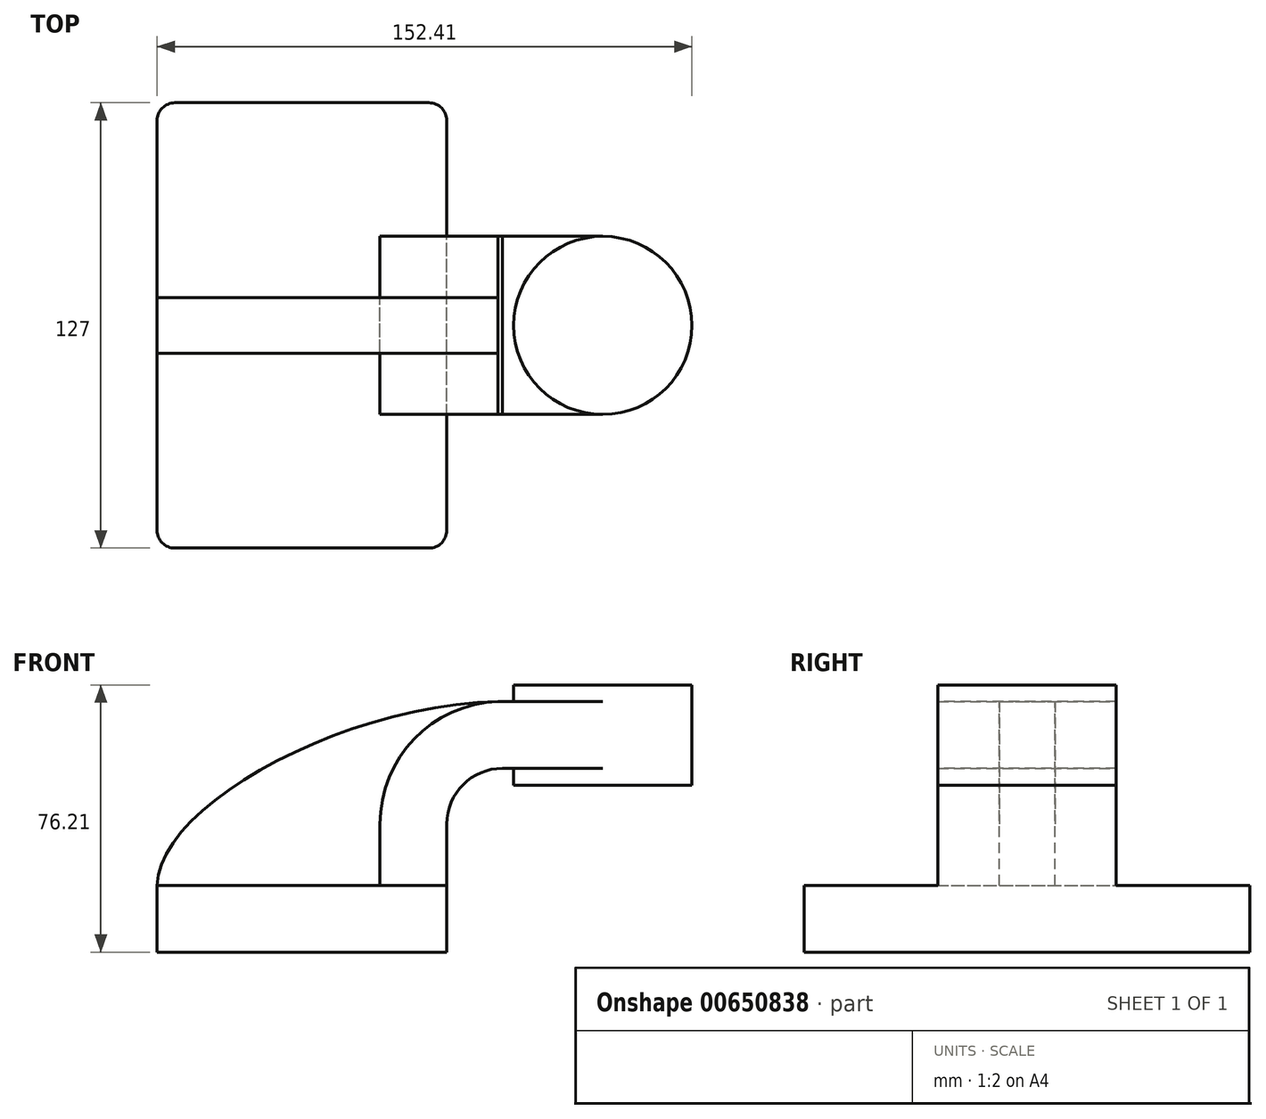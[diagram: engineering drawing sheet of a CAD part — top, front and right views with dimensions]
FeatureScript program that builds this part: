
annotation { "Feature Type Name" : "Feature", "Feature Type Description" : "" }
export const myFeature = defineFeature(function(context is Context, id is Id, definition is map)
    precondition{}
    {
        {
            var Q0;
            Q0=qCreatedBy(makeId("Front.planeOp"),FACE);
            var sketch = newSketch(context, id + "F0", { "sketchPlane" : qUnion([Q0])});
            skLineSegment(sketch, "E0.bottom", {"start": v(-41.28, -9.52) * mm, "end": v(41.28, -9.52) * mm});
            skLineSegment(sketch, "E0.top", {"start": v(-41.28, 9.53) * mm, "end": v(41.27, 9.53) * mm});
            skLineSegment(sketch, "E0.left", {"start": v(-41.27, -9.53) * mm, "end": v(-41.27, 9.52) * mm});
            skLineSegment(sketch, "E0.right", {"start": v(41.28, -9.53) * mm, "end": v(41.28, 9.52) * mm});
            skPoint(sketch, "E0.middle", {"position": v(0, 0) * mm});
            skLineSegment(sketch, "E1.bottom", {"start": v(60.32, 38.1) * mm, "end": v(111.12, 38.1) * mm});
            skLineSegment(sketch, "E1.top", {"start": v(60.32, 66.67) * mm, "end": v(111.12, 66.67) * mm});
            skLineSegment(sketch, "E1.left", {"start": v(60.32, 38.1) * mm, "end": v(60.32, 66.67) * mm});
            skLineSegment(sketch, "E1.right", {"start": v(111.12, 38.1) * mm, "end": v(111.12, 66.67) * mm});
            skPoint(sketch, "E1.middle", {"position": v(85.72, 52.39) * mm});
            skLineSegment(sketch, "E2", {"start": v(41.28, 9.52) * mm, "end": v(41.28, 27) * mm});
            skArc(sketch, "E3", {"start": v(41.27, 27) * mm, "mid": v(45.92, 38.23) * mm, "end": v(57.15, 42.88) * mm});
            skLineSegment(sketch, "E4", {"start": v(57.15, 42.88) * mm, "end": v(85.72, 42.88) * mm});
            skLineSegment(sketch, "E5.0", {"start": v(57.15, 61.93) * mm, "end": v(85.72, 61.93) * mm});
            skArc(sketch, "E5.1", {"start": v(22.22, 27) * mm, "mid": v(32.45, 51.7) * mm, "end": v(57.15, 61.93) * mm});
            skLineSegment(sketch, "E5.2", {"start": v(22.23, 9.53) * mm, "end": v(22.23, 27) * mm});
            skFitSpline(sketch, "E6", {"points": [v(-41.28, 9.53) * mm, v(57.15, 61.93) * mm], "startDerivative": vector(0.9, 67.4) * mm, "endDerivative": vector(137.17, 1.68) * mm});
            skLineSegment(sketch, "E7", {"start": v(85.72, 66.67) * mm, "end": v(85.72, 38.1) * mm});
            skSolve(sketch);
        }
        {
            var Q0;
            Q0=makeQuery(id+"F0.imprint","IMPRINT",FACE,{"disambiguationData":[TD([[makeQuery(id+"F0.imprint","IMPRINT",EDGE,{"derivedFrom":sQuery(id+"F0.wireOp",EDGE,"E0.bottom")}),1.0]])]});
            extrude(context, id + "F1", {"entities" : qUnion([Q0]), "endBound" : BoundingType.SYMMETRIC, "depth" : 127 * mm, "offsetDistance" : 25.4 * mm});
        }
        {
            var Q0;
            {var subQ1=sQuery(id+"F0.wireOp",EDGE,"E2");Q0=makeQuery(id+"F0.imprint","IMPRINT",FACE,{"disambiguationData":[TD([[makeQuery(id+"F0.imprint","IMPRINT",EDGE,{"derivedFrom":subQ1}),1.0]])]});}
            var Q1;
            {var subQ0=sQuery(id+"F0.wireOp",EDGE,"E4");var subQ1=sQuery(id+"F0.wireOp",EDGE,"E1.left");var subQ2=makeQuery(id+"F0.imprint","INTERSECT",VERTEX,{"derivedFrom":[subQ1,subQ0]});Q1=makeQuery(id+"F0.imprint","IMPRINT",FACE,{"disambiguationData":[TD([[makeQuery(id+"F0.imprint","IMPRINT",EDGE,{"disambiguationData":[TD([[subQ2,-1.0]])],"derivedFrom":subQ1}),-1.0]])]});}
            extrude(context, id + "F2", {"entities" : qUnion([Q0, Q1]), "operationType" : NewBodyOperationType.ADD, "endBound" : BoundingType.SYMMETRIC, "depth" : 50.8 * mm, "offsetDistance" : 25.4 * mm});
        }
        {
            var Q0;
            {var subQ3=sQuery(id+"F0.wireOp",EDGE,"E5.2");Q0=makeQuery(id+"F0.imprint","IMPRINT",FACE,{"disambiguationData":[TD([[makeQuery(id+"F0.imprint","IMPRINT",EDGE,{"derivedFrom":subQ3}),1.0]])]});}
            extrude(context, id + "F3", {"entities" : qUnion([Q0]), "endBound" : BoundingType.SYMMETRIC, "depth" : 15.88 * mm, "offsetDistance" : 25.4 * mm});
        }
        {
            var Q0;
            {var subQ4=sQuery(id+"F0.wireOp",EDGE,"E1.right");Q0=makeQuery(id+"F0.imprint","IMPRINT",FACE,{"disambiguationData":[TD([[makeQuery(id+"F0.imprint","IMPRINT",EDGE,{"derivedFrom":subQ4}),1.0]])]});}
            var Q1;
            Q1=sQuery(id+"F0.wireOp",EDGE,"E7");
            revolve(context, id + "F4", {"operationType" : NewBodyOperationType.ADD, "entities" : qUnion([Q0]), "axis" : qUnion([Q1]), "revolveType" : RevolveType.FULL});
        }
        {
            var Q0;
            Q0=makeQuery(id+"F1.opExtrude","CAP_EDGE",EDGE,{"disambiguationData":[OSD([sQuery(id+"F0.wireOp",EDGE,"E0.right")])],"isStart":false});
            var Q1;
            Q1=makeQuery(id+"F1.opExtrude","CAP_EDGE",EDGE,{"disambiguationData":[OSD([sQuery(id+"F0.wireOp",EDGE,"E0.left")])],"isStart":false});
            var Q2;
            Q2=makeQuery(id+"F1.opExtrude","CAP_EDGE",EDGE,{"disambiguationData":[OSD([sQuery(id+"F0.wireOp",EDGE,"E0.right")])],"isStart":true});
            var Q3;
            Q3=makeQuery(id+"F1.opExtrude","CAP_EDGE",EDGE,{"disambiguationData":[OSD([sQuery(id+"F0.wireOp",EDGE,"E0.left")])],"isStart":true});
            fillet(context, id + "F5", {"entities" : qUnion([Q0, Q1, Q2, Q3]), "radius" : 5.08 * mm, "tangentPropagation" : true, "allowEdgeOverflow" : false});
        }
    });
